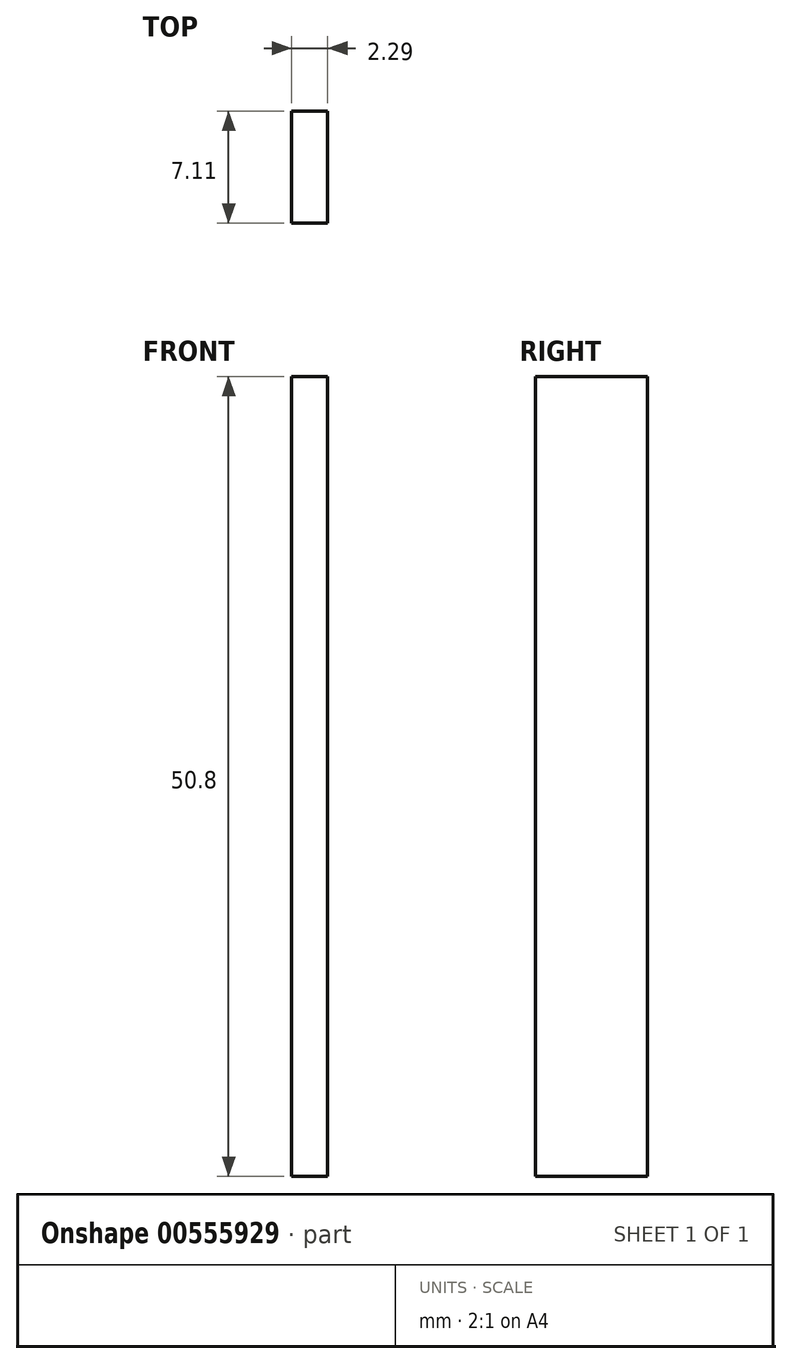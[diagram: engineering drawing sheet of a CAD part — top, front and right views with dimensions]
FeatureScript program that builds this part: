
annotation { "Feature Type Name" : "Feature", "Feature Type Description" : "" }
export const myFeature = defineFeature(function(context is Context, id is Id, definition is map)
    precondition{}
    {
        {
            var Q0;
            Q0=qCreatedBy(makeId("Top.planeOp"),FACE);
            var sketch = newSketch(context, id + "F0", { "sketchPlane" : qUnion([Q0])});
            skLineSegment(sketch, "E0.bottom", {"start": v(-2.29, 7.11) * mm, "end": v(0, 7.11) * mm});
            skLineSegment(sketch, "E0.top", {"start": v(-2.29, 0) * mm, "end": v(0, 0) * mm});
            skLineSegment(sketch, "E0.left", {"start": v(-2.29, 7.11) * mm, "end": v(-2.29, 0) * mm});
            skLineSegment(sketch, "E0.right", {"start": v(0, 7.11) * mm, "end": v(0, 0) * mm});
            skSolve(sketch);
        }
        {
            var Q0;
            Q0=makeQuery(id+"F0.imprint","IMPRINT",FACE,{"disambiguationData":[TD([[makeQuery(id+"F0.imprint","IMPRINT",EDGE,{"derivedFrom":sQuery(id+"F0.wireOp",EDGE,"E0.bottom")}),-1.0]])]});
            extrude(context, id + "F1", {"entities" : qUnion([Q0]), "depth" : 50.8 * mm, "offsetDistance" : 25.4 * mm});
        }
    });
